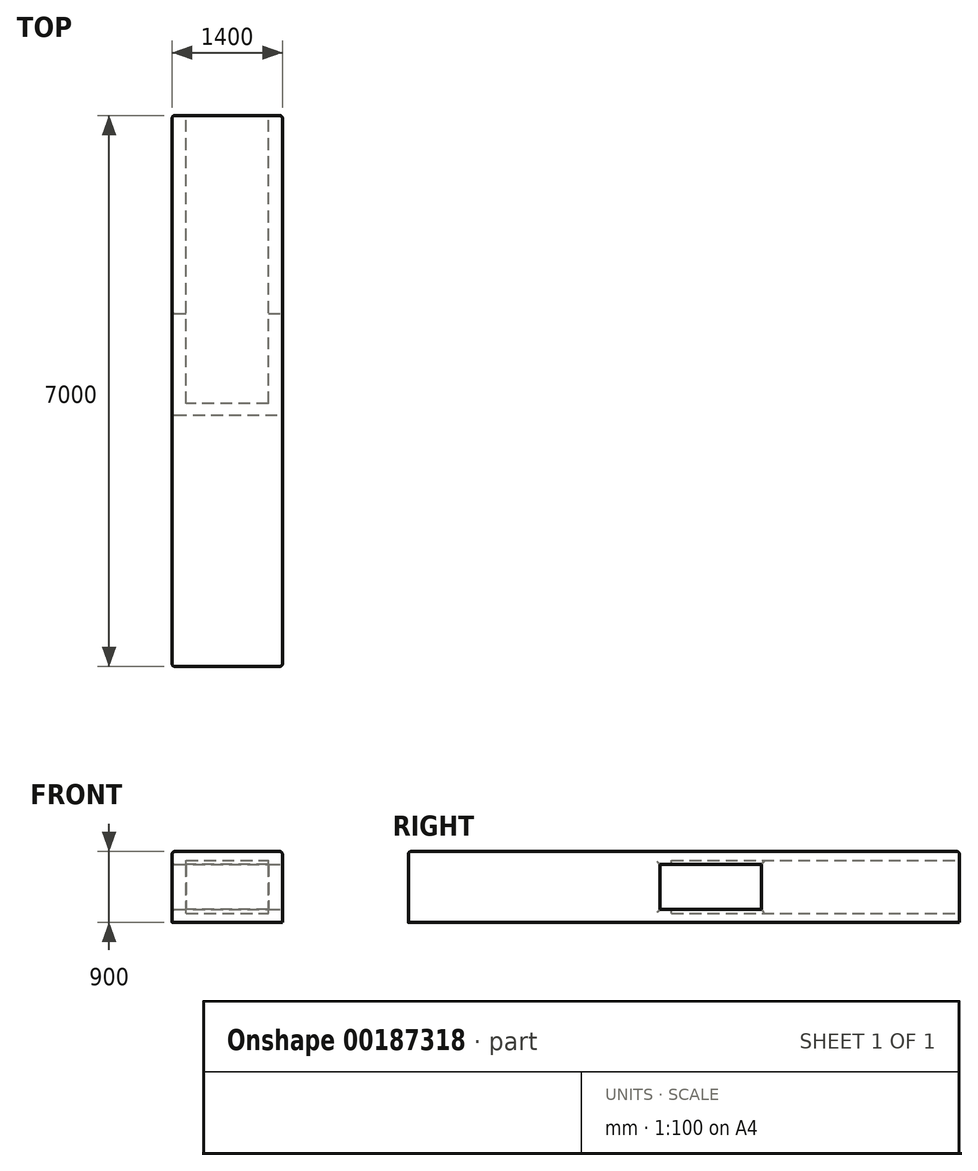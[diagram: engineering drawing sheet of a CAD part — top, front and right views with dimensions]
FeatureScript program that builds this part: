
annotation { "Feature Type Name" : "Feature", "Feature Type Description" : "" }
export const myFeature = defineFeature(function(context is Context, id is Id, definition is map)
    precondition{}
    {
        {
            var Q0;
            Q0=qCreatedBy(makeId("Front.planeOp"),FACE);
            var sketch = newSketch(context, id + "F0", { "sketchPlane" : qUnion([Q0])});
            skLineSegment(sketch, "E0.bottom", {"start": v(700, -450) * mm, "end": v(-700, -450) * mm});
            skLineSegment(sketch, "E0.top", {"start": v(700, 450) * mm, "end": v(-700, 450) * mm});
            skLineSegment(sketch, "E0.left", {"start": v(700, -450) * mm, "end": v(700, 450) * mm});
            skLineSegment(sketch, "E0.right", {"start": v(-700, -450) * mm, "end": v(-700, 450) * mm});
            skPoint(sketch, "E0.middle", {"position": v(0, 0) * mm});
            skSolve(sketch);
        }
        {
            var Q0;
            Q0 = qSketchRegion(id + "F0", true);
            extrude(context, id + "F1", {"entities" : qUnion([Q0]), "depth" : 7000 * mm});
        }
        {
            var Q0;
            Q0=qCreatedBy(makeId("Front.planeOp"),FACE);
            var sketch = newSketch(context, id + "F2", { "sketchPlane" : qUnion([Q0])});
            skLineSegment(sketch, "E1.bottom", {"start": v(-522.03, -334.48) * mm, "end": v(522.03, -334.48) * mm});
            skLineSegment(sketch, "E1.top", {"start": v(-522.03, 334.48) * mm, "end": v(522.03, 334.48) * mm});
            skLineSegment(sketch, "E1.left", {"start": v(-522.03, -334.48) * mm, "end": v(-522.03, 334.48) * mm});
            skLineSegment(sketch, "E1.right", {"start": v(522.03, -334.48) * mm, "end": v(522.03, 334.48) * mm});
            skPoint(sketch, "E1.middle", {"position": v(0, 0) * mm});
            skSolve(sketch);
        }
        {
            var Q0;
            Q0 = qSketchRegion(id + "F2", true);
            extrude(context, id + "F3", {"entities" : qUnion([Q0]), "operationType" : NewBodyOperationType.REMOVE, "depth" : 3657.6 * mm});
        }
        {
            var Q0;
            Q0=makeQuery(id+"F1.opExtrude","SWEPT_FACE",FACE,{"disambiguationData":[OSD([sQuery(id+"F0.wireOp",EDGE,"E0.left")])]});
            var sketch = newSketch(context, id + "F4", { "sketchPlane" : qUnion([Q0])});
            skLineSegment(sketch, "E2", {"start": v(-3657.6, 1037.22) * mm, "end": v(-3657.6, -785.01) * mm, "construction": true});
            skLineSegment(sketch, "E3", {"start": v(83.04, 0) * mm, "end": v(-3657.6, 0) * mm, "construction": true});
            skLineSegment(sketch, "E4.bottom", {"start": v(-2516.2, -286.67) * mm, "end": v(-3804.67, -286.67) * mm});
            skLineSegment(sketch, "E4.top", {"start": v(-2516.2, 286.67) * mm, "end": v(-3804.67, 286.67) * mm});
            skLineSegment(sketch, "E4.left", {"start": v(-2516.2, -286.67) * mm, "end": v(-2516.2, 286.67) * mm});
            skLineSegment(sketch, "E4.right", {"start": v(-3804.67, -286.67) * mm, "end": v(-3804.67, 286.67) * mm});
            skPoint(sketch, "E4.middle", {"position": v(-3160.44, 0) * mm});
            skSolve(sketch);
        }
        {
            var Q0;
            Q0 = qSketchRegion(id + "F4", true);
            extrude(context, id + "F5", {"entities" : qUnion([Q0]), "operationType" : NewBodyOperationType.REMOVE, "endBound" : BoundingType.THROUGH_ALL, "oppositeDirection" : true, "depth" : 25 * mm});
        }
        {
            var Q0;
            Q0=makeQuery(id+"F1.opExtrude","CAP_EDGE",EDGE,{"disambiguationData":[OSD([sQuery(id+"F0.wireOp",EDGE,"E0.top")])],"isStart":false});
            var Q1;
            Q1=makeQuery(id+"F1.opExtrude","CAP_EDGE",EDGE,{"disambiguationData":[OSD([sQuery(id+"F0.wireOp",EDGE,"E0.left")])],"isStart":false});
            var Q2;
            Q2=makeQuery(id+"F1.opExtrude","SWEPT_EDGE",EDGE,{"disambiguationData":[OSD([sQuery(id+"F0.wireOp",EDGE,"E0.top"),sQuery(id+"F0.wireOp",EDGE,"E0.left")])]});
            var Q3;
            Q3=makeQuery(id+"F1.opExtrude","CAP_EDGE",EDGE,{"disambiguationData":[OSD([sQuery(id+"F0.wireOp",EDGE,"E0.right")])],"isStart":false});
            var Q4;
            Q4=makeQuery(id+"F1.opExtrude","SWEPT_EDGE",EDGE,{"disambiguationData":[OSD([sQuery(id+"F0.wireOp",EDGE,"E0.top"),sQuery(id+"F0.wireOp",EDGE,"E0.right")])]});
            var Q5;
            Q5=makeQuery(id+"F1.opExtrude","CAP_EDGE",EDGE,{"disambiguationData":[OSD([sQuery(id+"F0.wireOp",EDGE,"E0.top")])],"isStart":true});
            var Q6;
            Q6=makeQuery(id+"F1.opExtrude","CAP_EDGE",EDGE,{"disambiguationData":[OSD([sQuery(id+"F0.wireOp",EDGE,"E0.left")])],"isStart":true});
            var Q7;
            Q7=makeQuery(id+"F1.opExtrude","CAP_EDGE",EDGE,{"disambiguationData":[OSD([sQuery(id+"F0.wireOp",EDGE,"E0.right")])],"isStart":true});
            fillet(context, id + "F6", {"entities" : qUnion([Q0, Q1, Q2, Q3, Q4, Q5, Q6, Q7]), "radius" : 35 * mm, "tangentPropagation" : true, "allowEdgeOverflow" : false});
        }
        {
            var Q0;
            Q0=makeQuery(id+"F3.boolean.opBoolean","COPY",EDGE,{"derivedFrom":makeQuery(id+"F3.opExtrude","CAP_EDGE",EDGE,{"disambiguationData":[OSD([sQuery(id+"F2.wireOp",EDGE,"E1.right")])],"isStart":true})});
            var Q1;
            Q1=makeQuery(id+"F3.boolean.opBoolean","COPY",EDGE,{"derivedFrom":makeQuery(id+"F3.opExtrude","CAP_EDGE",EDGE,{"disambiguationData":[OSD([sQuery(id+"F2.wireOp",EDGE,"E1.top")])],"isStart":true})});
            var Q2;
            Q2=makeQuery(id+"F3.boolean.opBoolean","COPY",EDGE,{"derivedFrom":makeQuery(id+"F3.opExtrude","CAP_EDGE",EDGE,{"disambiguationData":[OSD([sQuery(id+"F2.wireOp",EDGE,"E1.left")])],"isStart":true})});
            var Q3;
            Q3=makeQuery(id+"F5.boolean.opBoolean","COPY",EDGE,{"derivedFrom":makeQuery(id+"F5.opExtrude","CAP_EDGE",EDGE,{"disambiguationData":[OSD([sQuery(id+"F4.wireOp",EDGE,"E4.right")])],"isStart":true})});
            var Q4;
            Q4=makeQuery(id+"F5.boolean.opBoolean","COPY",EDGE,{"derivedFrom":makeQuery(id+"F5.opExtrude","CAP_EDGE",EDGE,{"disambiguationData":[OSD([sQuery(id+"F4.wireOp",EDGE,"E4.bottom")])],"isStart":true})});
            var Q5;
            Q5=makeQuery(id+"F5.boolean.opBoolean","COPY",EDGE,{"derivedFrom":makeQuery(id+"F5.opExtrude","CAP_EDGE",EDGE,{"disambiguationData":[OSD([sQuery(id+"F4.wireOp",EDGE,"E4.left")])],"isStart":true})});
            var Q6;
            Q6=makeQuery(id+"F5.boolean.opBoolean","COPY",EDGE,{"derivedFrom":makeQuery(id+"F5.opExtrude","CAP_EDGE",EDGE,{"disambiguationData":[OSD([sQuery(id+"F4.wireOp",EDGE,"E4.top")])],"isStart":true})});
            var Q7;
            Q7=makeQuery(id+"F5.boolean.opBoolean","INTERSECT",EDGE,{"derivedFrom":[makeQuery(id+"F1.opExtrude","SWEPT_FACE",FACE,{"disambiguationData":[OSD([sQuery(id+"F0.wireOp",EDGE,"E0.right")])]}),makeQuery(id+"F5.opExtrude","SWEPT_FACE",FACE,{"disambiguationData":[OSD([sQuery(id+"F4.wireOp",EDGE,"E4.bottom")])]})]});
            var Q8;
            Q8=makeQuery(id+"F5.boolean.opBoolean","INTERSECT",EDGE,{"derivedFrom":[makeQuery(id+"F1.opExtrude","SWEPT_FACE",FACE,{"disambiguationData":[OSD([sQuery(id+"F0.wireOp",EDGE,"E0.right")])]}),makeQuery(id+"F5.opExtrude","SWEPT_FACE",FACE,{"disambiguationData":[OSD([sQuery(id+"F4.wireOp",EDGE,"E4.left")])]})]});
            var Q9;
            Q9=makeQuery(id+"F5.boolean.opBoolean","INTERSECT",EDGE,{"derivedFrom":[makeQuery(id+"F1.opExtrude","SWEPT_FACE",FACE,{"disambiguationData":[OSD([sQuery(id+"F0.wireOp",EDGE,"E0.right")])]}),makeQuery(id+"F5.opExtrude","SWEPT_FACE",FACE,{"disambiguationData":[OSD([sQuery(id+"F4.wireOp",EDGE,"E4.top")])]})]});
            var Q10;
            Q10=makeQuery(id+"F5.boolean.opBoolean","INTERSECT",EDGE,{"derivedFrom":[makeQuery(id+"F1.opExtrude","SWEPT_FACE",FACE,{"disambiguationData":[OSD([sQuery(id+"F0.wireOp",EDGE,"E0.right")])]}),makeQuery(id+"F5.opExtrude","SWEPT_FACE",FACE,{"disambiguationData":[OSD([sQuery(id+"F4.wireOp",EDGE,"E4.right")])]})]});
            fillet(context, id + "F7", {"entities" : qUnion([Q0, Q1, Q2, Q3, Q4, Q5, Q6, Q7, Q8, Q9, Q10]), "radius" : 35 * mm, "tangentPropagation" : true, "allowEdgeOverflow" : false});
        }
    });
